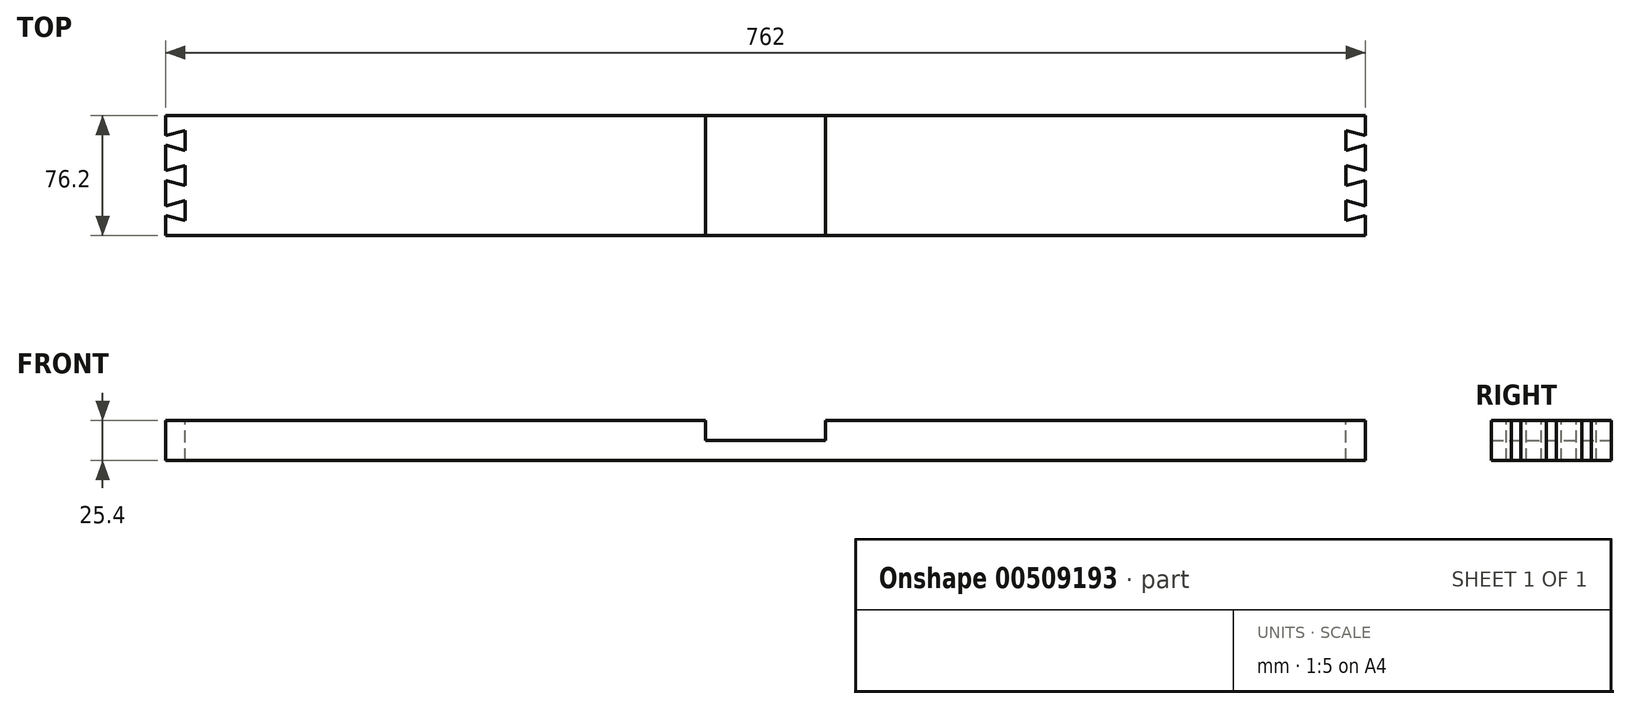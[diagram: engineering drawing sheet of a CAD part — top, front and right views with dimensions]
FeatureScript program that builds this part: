
annotation { "Feature Type Name" : "Feature", "Feature Type Description" : "" }
export const myFeature = defineFeature(function(context is Context, id is Id, definition is map)
    precondition{}
    {
        {
            var Q0;
            Q0=qCreatedBy(makeId("Front.planeOp"),FACE);
            var sketch = newSketch(context, id + "F0", { "sketchPlane" : qUnion([Q0])});
            skLineSegment(sketch, "E0.bottom", {"start": v(-381, 12.7) * mm, "end": v(-38.1, 12.7) * mm});
            skLineSegment(sketch, "E0.top", {"start": v(-381, -12.7) * mm, "end": v(381, -12.7) * mm});
            skLineSegment(sketch, "E0.left", {"start": v(-381, 12.7) * mm, "end": v(-381, -12.7) * mm});
            skLineSegment(sketch, "E0.right", {"start": v(381, 12.7) * mm, "end": v(381, -12.7) * mm});
            skPoint(sketch, "E0.middle", {"position": v(0, 0) * mm});
            skLineSegment(sketch, "E1", {"start": v(-38.1, 12.7) * mm, "end": v(-38.1, 0) * mm});
            skPoint(sketch, "E1.endSnap0", {"position": v(-381, 0) * mm});
            skLineSegment(sketch, "E2", {"start": v(-38.1, 0) * mm, "end": v(38.1, 0) * mm});
            skLineSegment(sketch, "E3", {"start": v(38.1, 0) * mm, "end": v(38.1, 12.7) * mm});
            skLineSegment(sketch, "E4.trimOffspring", {"start": v(38.1, 12.7) * mm, "end": v(381, 12.7) * mm});
            skSolve(sketch);
        }
        {
            var Q0;
            Q0=makeQuery(id+"F0.imprint","IMPRINT",FACE,{"disambiguationData":[TD([[makeQuery(id+"F0.imprint","IMPRINT",EDGE,{"derivedFrom":sQuery(id+"F0.wireOp",EDGE,"E0.bottom")}),-1.0]])]});
            extrude(context, id + "F1", {"entities" : qUnion([Q0]), "endBound" : BoundingType.SYMMETRIC, "depth" : 76.2 * mm});
        }
        {
            var Q0;
            Q0=makeQuery(id+"F1.opExtrude","SWEPT_FACE",FACE,{"disambiguationData":[OSD([sQuery(id+"F0.wireOp",EDGE,"E4.trimOffspring")])]});
            var sketch = newSketch(context, id + "F2", { "sketchPlane" : qUnion([Q0])});
            skLineSegment(sketch, "E5", {"start": v(381, 25.4) * mm, "end": v(368.73, 28.69) * mm});
            skLineSegment(sketch, "E6", {"start": v(368.73, 28.69) * mm, "end": v(368.73, 15.99) * mm});
            skLineSegment(sketch, "E7", {"start": v(368.73, 15.99) * mm, "end": v(381, 19.27) * mm});
            skLineSegment(sketch, "E8", {"start": v(381, -25.4) * mm, "end": v(368.73, -28.69) * mm});
            skLineSegment(sketch, "E9", {"start": v(368.73, -28.69) * mm, "end": v(368.73, -15.99) * mm});
            skLineSegment(sketch, "E10", {"start": v(368.73, -15.99) * mm, "end": v(381, -19.27) * mm});
            skLineSegment(sketch, "E11", {"start": v(381, 3.06) * mm, "end": v(368.73, 6.35) * mm});
            skLineSegment(sketch, "E12", {"start": v(368.73, 6.35) * mm, "end": v(368.73, -6.35) * mm});
            skLineSegment(sketch, "E13", {"start": v(368.73, -6.35) * mm, "end": v(381, -3.06) * mm});
            skLineSegment(sketch, "E14", {"start": v(381, 25.4) * mm, "end": v(381, 19.27) * mm});
            skLineSegment(sketch, "E15", {"start": v(381, 3.06) * mm, "end": v(381, -3.06) * mm});
            skLineSegment(sketch, "E16", {"start": v(381, -19.27) * mm, "end": v(381, -25.4) * mm});
            skLineSegment(sketch, "E17.MirrorCS", {"start": v(-368.73, 28.69) * mm, "end": v(-368.73, 15.99) * mm});
            skLineSegment(sketch, "E18.MirrorCS", {"start": v(-368.73, 15.99) * mm, "end": v(-381, 19.27) * mm});
            skLineSegment(sketch, "E19.MirrorCS", {"start": v(-381, 25.4) * mm, "end": v(-381, 19.27) * mm});
            skLineSegment(sketch, "E20.MirrorCS", {"start": v(-381, 25.4) * mm, "end": v(-368.73, 28.69) * mm});
            skLineSegment(sketch, "E21.MirrorCS", {"start": v(-381, 3.06) * mm, "end": v(-368.73, 6.35) * mm});
            skLineSegment(sketch, "E22.MirrorCS", {"start": v(-368.73, 6.35) * mm, "end": v(-368.73, -6.35) * mm});
            skLineSegment(sketch, "E23.MirrorCS", {"start": v(-368.73, -6.35) * mm, "end": v(-381, -3.06) * mm});
            skLineSegment(sketch, "E24.MirrorCS", {"start": v(-381, 3.06) * mm, "end": v(-381, -3.06) * mm});
            skLineSegment(sketch, "E25.MirrorCS", {"start": v(-368.73, -15.99) * mm, "end": v(-381, -19.27) * mm});
            skLineSegment(sketch, "E26.MirrorCS", {"start": v(-368.73, -28.69) * mm, "end": v(-368.73, -15.99) * mm});
            skLineSegment(sketch, "E27.MirrorCS", {"start": v(-381, -19.27) * mm, "end": v(-381, -25.4) * mm});
            skLineSegment(sketch, "E28.MirrorCS", {"start": v(-381, -25.4) * mm, "end": v(-368.73, -28.69) * mm});
            skSolve(sketch);
        }
        {
            var Q0;
            Q0=makeQuery(id+"F2.imprint","IMPRINT",FACE,{"disambiguationData":[TD([[makeQuery(id+"F2.imprint","IMPRINT",EDGE,{"derivedFrom":sQuery(id+"F2.wireOp",EDGE,"E17.MirrorCS")}),-1.0]])]});
            var Q1;
            Q1=makeQuery(id+"F2.imprint","IMPRINT",FACE,{"disambiguationData":[TD([[makeQuery(id+"F2.imprint","IMPRINT",EDGE,{"derivedFrom":sQuery(id+"F2.wireOp",EDGE,"E21.MirrorCS")}),-1.0]])]});
            var Q2;
            Q2=makeQuery(id+"F2.imprint","IMPRINT",FACE,{"disambiguationData":[TD([[makeQuery(id+"F2.imprint","IMPRINT",EDGE,{"derivedFrom":sQuery(id+"F2.wireOp",EDGE,"E25.MirrorCS")}),1.0]])]});
            var Q3;
            Q3=makeQuery(id+"F2.imprint","IMPRINT",FACE,{"disambiguationData":[TD([[makeQuery(id+"F2.imprint","IMPRINT",EDGE,{"derivedFrom":sQuery(id+"F2.wireOp",EDGE,"E5")}),1.0]])]});
            var Q4;
            Q4=makeQuery(id+"F2.imprint","IMPRINT",FACE,{"disambiguationData":[TD([[makeQuery(id+"F2.imprint","IMPRINT",EDGE,{"derivedFrom":sQuery(id+"F2.wireOp",EDGE,"E11")}),1.0]])]});
            var Q5;
            Q5=makeQuery(id+"F2.imprint","IMPRINT",FACE,{"disambiguationData":[TD([[makeQuery(id+"F2.imprint","IMPRINT",EDGE,{"derivedFrom":sQuery(id+"F2.wireOp",EDGE,"E8")}),-1.0]])]});
            extrude(context, id + "F3", {"entities" : qUnion([Q0, Q1, Q2, Q3, Q4, Q5]), "operationType" : NewBodyOperationType.REMOVE, "endBound" : BoundingType.THROUGH_ALL, "oppositeDirection" : true, "depth" : 25.4 * mm});
        }
    });
